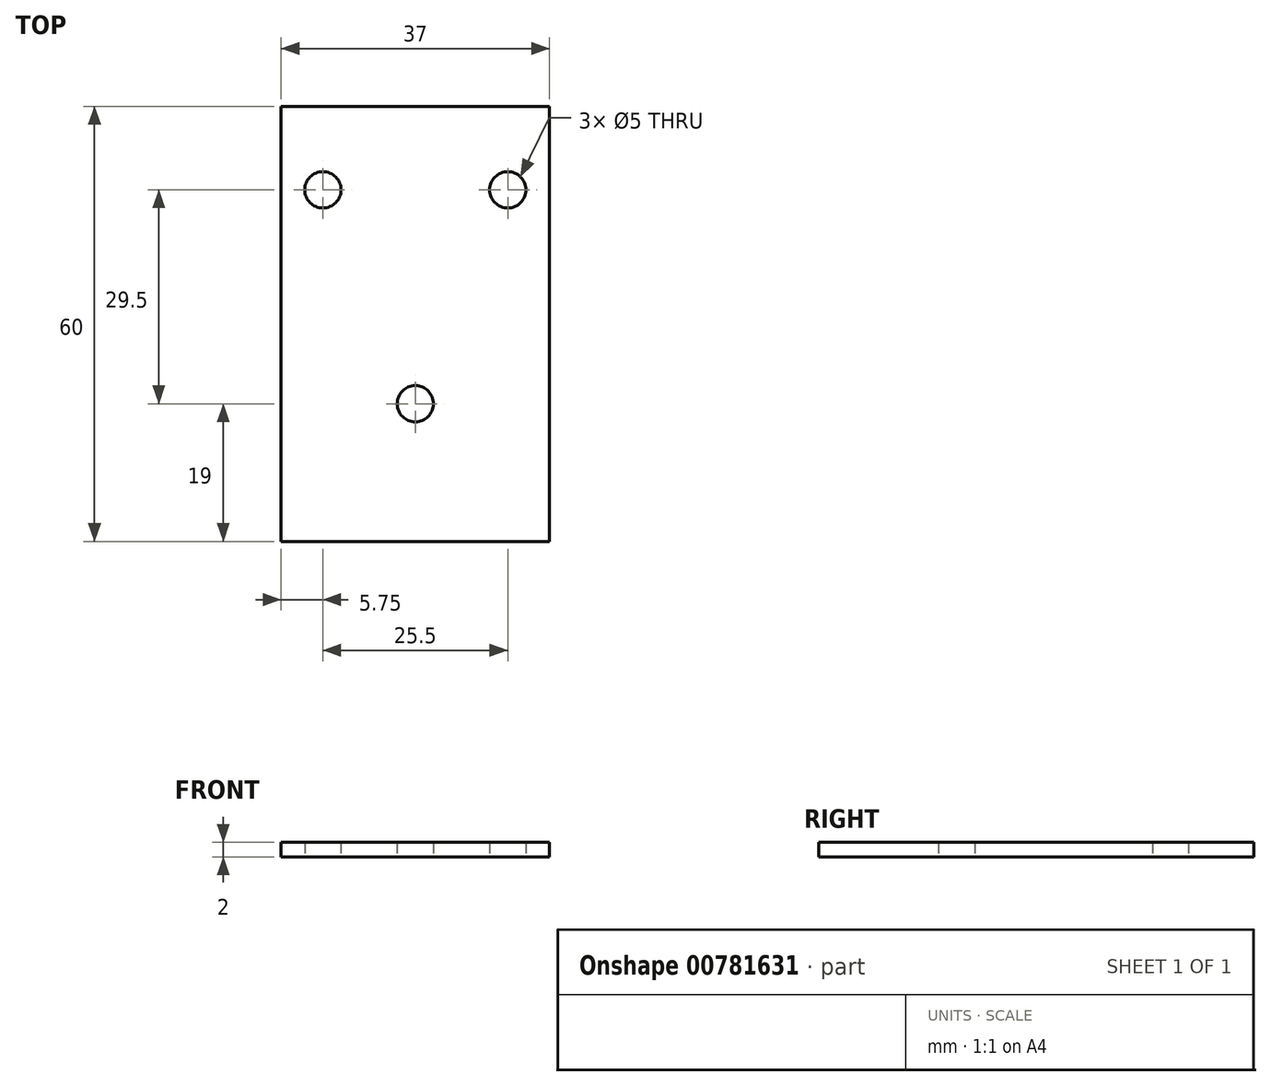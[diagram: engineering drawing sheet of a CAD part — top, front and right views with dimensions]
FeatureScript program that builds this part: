
annotation { "Feature Type Name" : "Feature", "Feature Type Description" : "" }
export const myFeature = defineFeature(function(context is Context, id is Id, definition is map)
    precondition{}
    {
        {
            var Q0;
            Q0=qCreatedBy(makeId("Top.planeOp"),FACE);
            var sketch = newSketch(context, id + "F0", { "sketchPlane" : qUnion([Q0])});
            skLineSegment(sketch, "E0.bottom", {"start": v(18.5, -30) * mm, "end": v(-18.5, -30) * mm});
            skLineSegment(sketch, "E0.top", {"start": v(18.5, 30) * mm, "end": v(-18.5, 30) * mm});
            skLineSegment(sketch, "E0.left", {"start": v(18.5, -30) * mm, "end": v(18.5, 30) * mm});
            skLineSegment(sketch, "E0.right", {"start": v(-18.5, -30) * mm, "end": v(-18.5, 30) * mm});
            skPoint(sketch, "E0.middle", {"position": v(0, 0) * mm});
            skCircle(sketch, "E1", {"center": v(-12.75, 18.5) * mm, "radius": 2.5 * mm});
            skCircle(sketch, "E2", {"center": v(12.75, 18.5) * mm, "radius": 2.5 * mm});
            skCircle(sketch, "E3", {"center": v(0, -11) * mm, "radius": 2.5 * mm});
            skLineSegment(sketch, "E4", {"start": v(-12.75, 18.5) * mm, "end": v(12.75, 18.5) * mm, "construction": true});
            skPoint(sketch, "E5", {"position": v(0, 18.5) * mm});
            skSolve(sketch);
        }
        {
            var Q0;
            Q0=makeQuery(id+"F0.imprint","IMPRINT",FACE,{"disambiguationData":[TD([[makeQuery(id+"F0.imprint","IMPRINT",EDGE,{"derivedFrom":sQuery(id+"F0.wireOp",EDGE,"E0.bottom")}),-1.0]])]});
            extrude(context, id + "F1", {"entities" : qUnion([Q0]), "depth" : 2 * mm, "offsetDistance" : 25 * mm});
        }
    });
